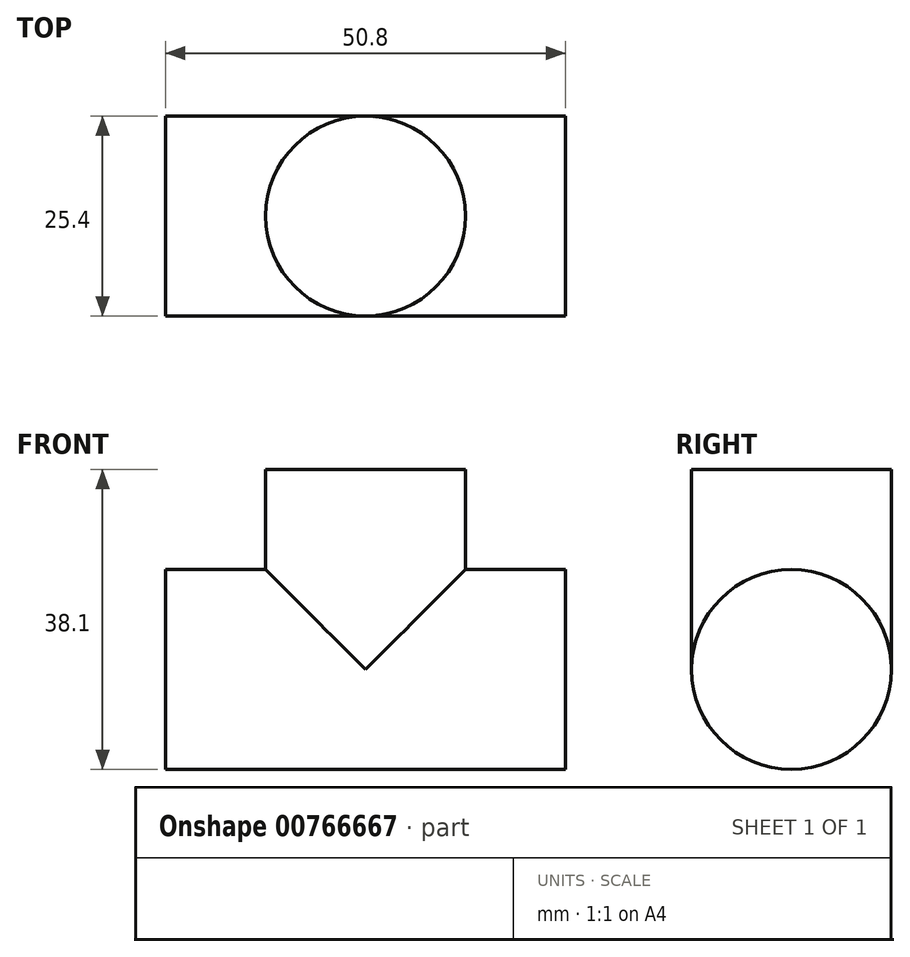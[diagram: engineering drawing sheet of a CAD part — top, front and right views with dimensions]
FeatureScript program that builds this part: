
annotation { "Feature Type Name" : "Feature", "Feature Type Description" : "" }
export const myFeature = defineFeature(function(context is Context, id is Id, definition is map)
    precondition{}
    {
        {
            var Q0;
            Q0=qCreatedBy(makeId("Front.planeOp"),FACE);
            var sketch = newSketch(context, id + "F0", { "sketchPlane" : qUnion([Q0])});
            skCircle(sketch, "E0", {"center": v(0, 0) * mm, "radius": 12.7 * mm});
            skSolve(sketch);
        }
        {
            var Q0;
            Q0=sQuery(id+"F0.wireOp",EDGE,"E0");
            extrude(context, id + "F1", {"bodyType" : ToolBodyType.SURFACE, "surfaceEntities" : qUnion([Q0]), "endBound" : BoundingType.SYMMETRIC, "depth" : 50.8 * mm, "offsetDistance" : 25.4 * mm});
        }
        {
            var Q0;
            Q0=qCreatedBy(makeId("Top.planeOp"),FACE);
            var sketch = newSketch(context, id + "F2", { "sketchPlane" : qUnion([Q0])});
            skCircle(sketch, "E1", {"center": v(0, 0) * mm, "radius": 12.7 * mm});
            skSolve(sketch);
        }
        {
            var Q0;
            Q0 = qSketchRegion(id + "F2", true);
            extrude(context, id + "F3", {"entities" : qUnion([Q0]), "depth" : 25.4 * mm, "offsetDistance" : 25.4 * mm});
        }
        {
            var Q0;
            Q0=makeQuery(id+"F1.opExtrude","SWEPT_BODY",BODY,{"disambiguationData":[OSD([sQuery(id+"F0.wireOp",EDGE,"E0")])]});
            deleteBodies(context, id + "F4", {"entities" : qUnion([Q0])});
        }
        {
            var Q0;
            Q0=qCreatedBy(makeId("Right.planeOp"),FACE);
            var sketch = newSketch(context, id + "F5", { "sketchPlane" : qUnion([Q0])});
            skCircle(sketch, "E2", {"center": v(0, 0) * mm, "radius": 12.7 * mm});
            skSolve(sketch);
        }
        {
            var Q0;
            Q0 = qSketchRegion(id + "F5", true);
            extrude(context, id + "F6", {"entities" : qUnion([Q0]), "operationType" : NewBodyOperationType.ADD, "endBound" : BoundingType.SYMMETRIC, "depth" : 50.8 * mm, "offsetDistance" : 25.4 * mm});
        }
    });
